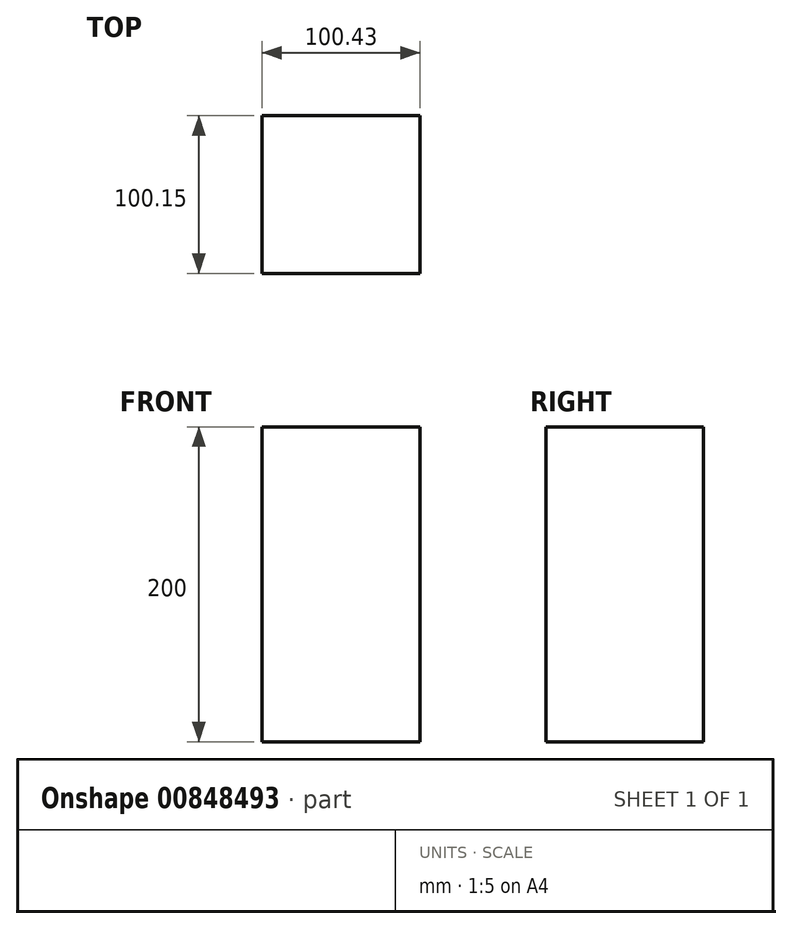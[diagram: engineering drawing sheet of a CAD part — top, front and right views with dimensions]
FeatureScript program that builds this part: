
annotation { "Feature Type Name" : "Feature", "Feature Type Description" : "" }
export const myFeature = defineFeature(function(context is Context, id is Id, definition is map)
    precondition{}
    {
        {
            var Q0;
            Q0=qCreatedBy(makeId("Top.planeOp"),FACE);
            var sketch = newSketch(context, id + "F0", { "sketchPlane" : qUnion([Q0])});
            skLineSegment(sketch, "E0", {"start": v(-48.87, -45.12) * mm, "end": v(-48.87, 55.03) * mm});
            skLineSegment(sketch, "E1", {"start": v(-48.87, 55.03) * mm, "end": v(51.56, 55.03) * mm});
            skLineSegment(sketch, "E2", {"start": v(51.56, 55.03) * mm, "end": v(51.56, -45.12) * mm});
            skLineSegment(sketch, "E3", {"start": v(51.56, -45.12) * mm, "end": v(-48.87, -45.12) * mm});
            skSolve(sketch);
        }
        {
            var Q0;
            Q0=makeQuery(id+"F0.imprint","IMPRINT",FACE,{"disambiguationData":[TD([[makeQuery(id+"F0.imprint","IMPRINT",EDGE,{"derivedFrom":sQuery(id+"F0.wireOp",EDGE,"E0")}),-1.0]])]});
            extrude(context, id + "F1", {"entities" : qUnion([Q0]), "depth" : 200 * mm, "offsetDistance" : 25 * mm});
        }
    });
